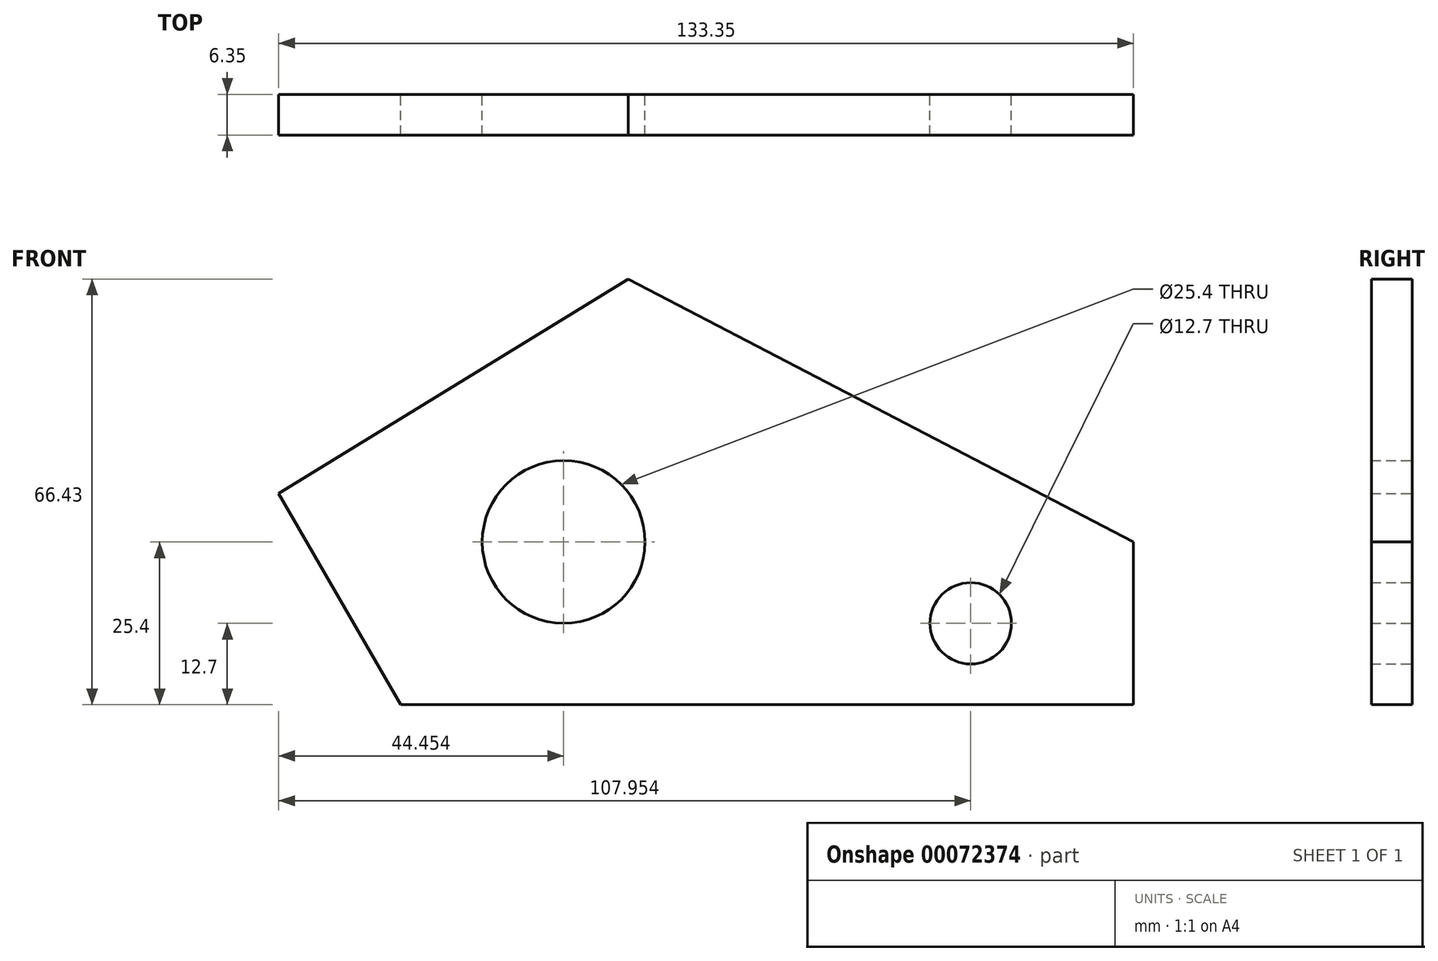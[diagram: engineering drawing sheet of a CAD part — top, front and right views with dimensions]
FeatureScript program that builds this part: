
annotation { "Feature Type Name" : "Feature", "Feature Type Description" : "" }
export const myFeature = defineFeature(function(context is Context, id is Id, definition is map)
    precondition{}
    {
        {
            var Q0;
            Q0=qCreatedBy(makeId("Front.planeOp"),FACE);
            var sketch = newSketch(context, id + "F0", { "sketchPlane" : qUnion([Q0])});
            skLineSegment(sketch, "E0", {"start": v(-55.16, 0) * mm, "end": v(59.14, 0) * mm});
            skLineSegment(sketch, "E1", {"start": v(59.14, 0) * mm, "end": v(59.14, 25.4) * mm});
            skLineSegment(sketch, "E2", {"start": v(59.14, 25.4) * mm, "end": v(-19.72, 66.43) * mm});
            skLineSegment(sketch, "E3", {"start": v(-19.72, 66.43) * mm, "end": v(-74.2, 33) * mm});
            skLineSegment(sketch, "E4", {"start": v(-74.2, 33) * mm, "end": v(-55.16, 0) * mm});
            skCircle(sketch, "E5", {"center": v(-29.76, 25.4) * mm, "radius": 12.7 * mm});
            skCircle(sketch, "E6", {"center": v(33.74, 12.7) * mm, "radius": 6.35 * mm});
            skSolve(sketch);
        }
        {
            var Q0;
            Q0=makeQuery(id+"F0.imprint","IMPRINT",FACE,{"disambiguationData":[TD([[makeQuery(id+"F0.imprint","IMPRINT",EDGE,{"derivedFrom":sQuery(id+"F0.wireOp",EDGE,"E0")}),1.0]])]});
            extrude(context, id + "F1", {"entities" : qUnion([Q0]), "depth" : 6.35 * mm});
        }
    });
